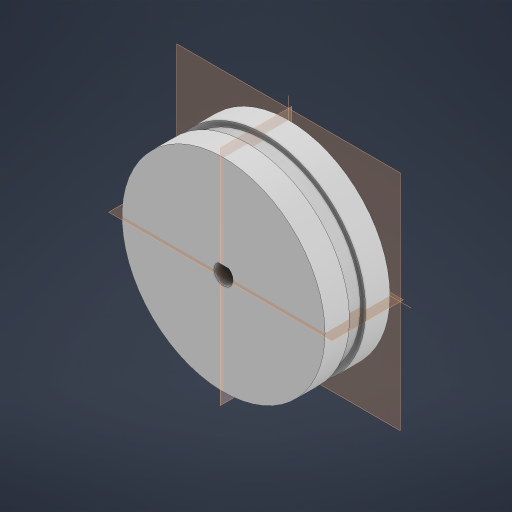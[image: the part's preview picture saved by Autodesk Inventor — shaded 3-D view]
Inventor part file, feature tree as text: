
AUTODESK INVENTOR PART (.ipt)
format: ipt  version: 2024.1 (Build 281209000, 209)  size: 224,256 bytes
history: native  units: in
note: dims shown in document units (in); Inventor stores cm internally (conversion verified against a paired STEP export)
features: sketch x2, extrude x1, revolve x1
ambient origin geometry x8: Origin, YZ Plane, XZ Plane, XY Plane, X Axis, Y Axis, Z Axis, Center Point
bodies: Solid1 (feature_tree)
feature tree (4):
  extrude  "Extrusion1"  Depth=0.2362in
  revolve  "Revolution1"  [1 undecoded]
  sketch  "Sketch1"  dims[d0=2.5in d1=0.2362in]
  sketch  "Sketch2"  dims[d2=0.2165in d3=0.8in d4=0.0in d5=0.2in d6=0.0625in d7=0.3in d8=90.0deg]
note: 1 required parameter value undecoded (feature->parameter linkage not recoverable at this tier; creation-order binding heuristic only, values carry confidence <= 0.55)
